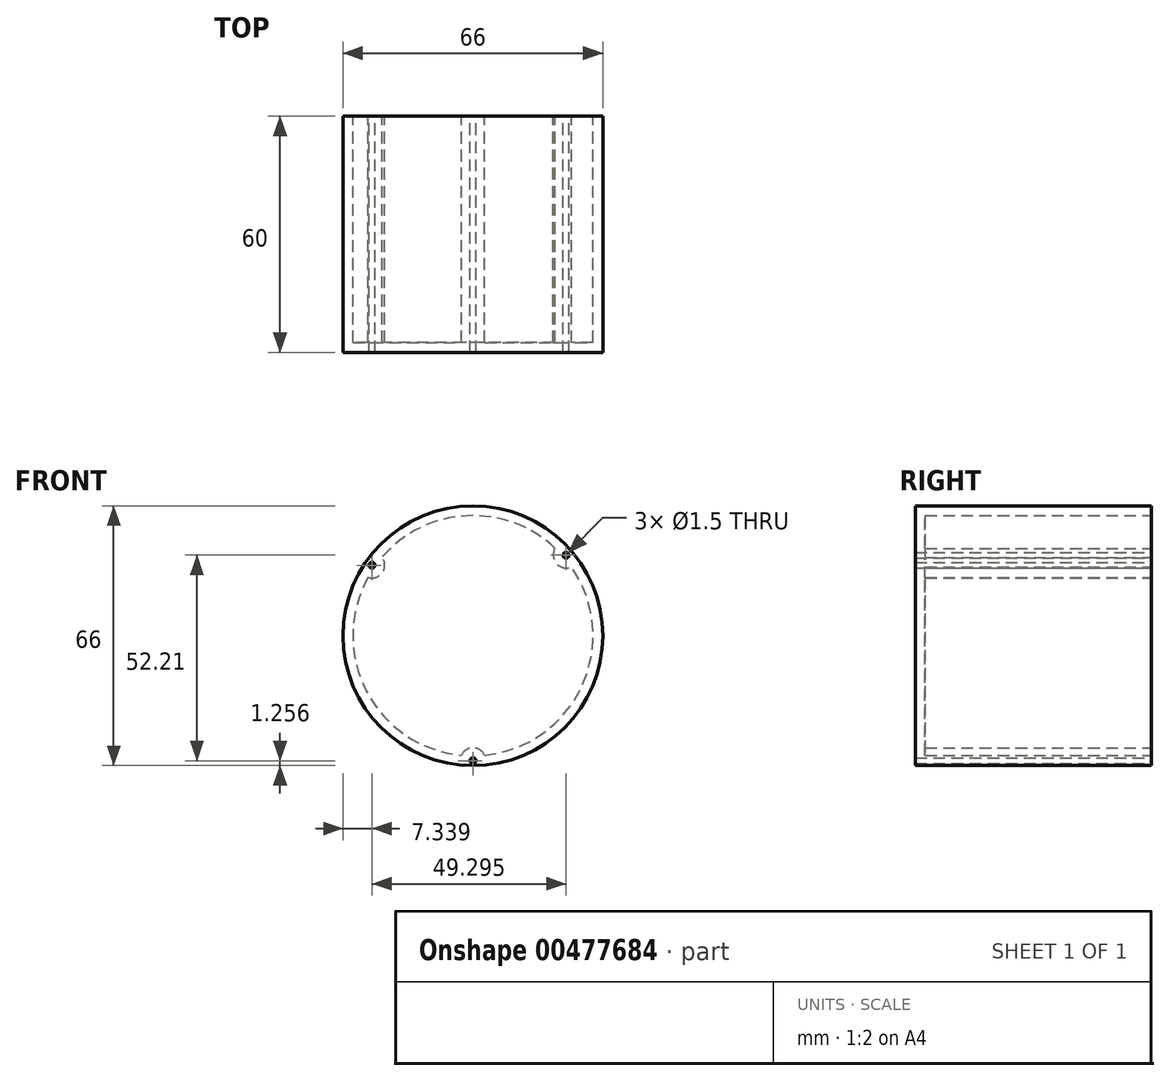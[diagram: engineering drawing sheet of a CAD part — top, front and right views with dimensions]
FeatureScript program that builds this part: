
annotation { "Feature Type Name" : "Feature", "Feature Type Description" : "" }
export const myFeature = defineFeature(function(context is Context, id is Id, definition is map)
    precondition{}
    {
        {
            var Q0;
            Q0=qCreatedBy(makeId("Front.planeOp"),FACE);
            var sketch = newSketch(context, id + "F0", { "sketchPlane" : qUnion([Q0])});
            skCircle(sketch, "E0", {"center": v(0, 0) * mm, "radius": 33 * mm});
            skCircle(sketch, "E1", {"center": v(0, -31.74) * mm, "radius": 0.75 * mm});
            skCircle(sketch, "E2", {"center": v(-25.66, 17.9) * mm, "radius": 0.75 * mm});
            skCircle(sketch, "E3", {"center": v(23.63, 20.47) * mm, "radius": 0.75 * mm});
            skCircle(sketch, "E4", {"center": v(0, 0) * mm, "radius": 30 * mm});
            skSolve(sketch);
        }
        {
            var Q0;
            Q0=makeQuery(id+"F0.imprint","IMPRINT",FACE,{"disambiguationData":[TD([[makeQuery(id+"F0.imprint","IMPRINT",EDGE,{"derivedFrom":sQuery(id+"F0.wireOp",EDGE,"E0")}),1.0]])]});
            var Q1;
            Q1=makeQuery(id+"F0.imprint","IMPRINT",FACE,{"disambiguationData":[TD([[makeQuery(id+"F0.imprint","IMPRINT",EDGE,{"derivedFrom":sQuery(id+"F0.wireOp",EDGE,"E4")}),1.0]])]});
            extrude(context, id + "F1", {"entities" : qUnion([Q0, Q1]), "depth" : 60 * mm});
        }
        {
            var Q0;
            Q0=qSketchRegion(id+"F0",true);
            extrude(context, id + "F2", {"entities" : qUnion([Q0]), "operationType" : NewBodyOperationType.ADD, "depth" : 3 * mm});
        }
        {
            var Q0;
            Q0=makeQuery(id+"F1.opExtrude","CAP_FACE",FACE,{"disambiguationData":[OSD([sQuery(id+"F0.wireOp",EDGE,"E0"),sQuery(id+"F0.wireOp",EDGE,"E1"),sQuery(id+"F0.wireOp",EDGE,"E2"),sQuery(id+"F0.wireOp",EDGE,"E3")])],"isStart":true});
            shell(context, id + "F3", {"entities" : qUnion([Q0]), "thickness" : 2.5 * mm});
        }
    });
